# Revit family: xFaucet_Pull_Down-American_Standard-Beale-4931.360
name_source: partatom
category: Plumbing Fixtures
revit_build: Autodesk Revit 2014 (Build: 20130308_1515(x64)
units: mm (PartAtom-declared; Revit-internal decimal feet)

## types (1)
- 4931.360
    ADA Compliant = Yes
    Assembly Code = D2020300
    CW Connection = Yes
    CWFU = 1.5
    Default Elevation = 0"
    Description = Beale™ Pull-Down Kitchen Faucet with MeasureFill™ Technology
    Finish = Metal-American Standard-002-Polished Chrome
    Flow Rate = 1.5 gpm (5.7L/min)
    HW Connection = Yes
    HWFU = 1.5
    Height = 17 5/8"
    Installation Type = Deck Mounted
    Length = 10 1/2"
    Manufacturer = American Standard
    Material = Metal-American Standard-002-Polished Chrome
    Model = 4931.360
    Price = Prices may vary. Please consult Manufacturer Representative for most up-to-date price list.
    Specification = Single control kitchen pull-down faucet shall feature a dial ring with MeasureFill™ technology, a high arc brass swivel spout with pull-down two-function spray, and metal lever handle. Shall also feature 35 mm washerless ceramic disc valve cartridge and flexible nylon supply hoses.
    URL = http://www.americanstandard-us.com
    Vent Connection = No
    WFU = 2
    Waste Connection = No
    Width = 1 1/2"

## geometry (parser evidence)
native form markers: Sweep x1
no freeform markers — native parametric forms only
